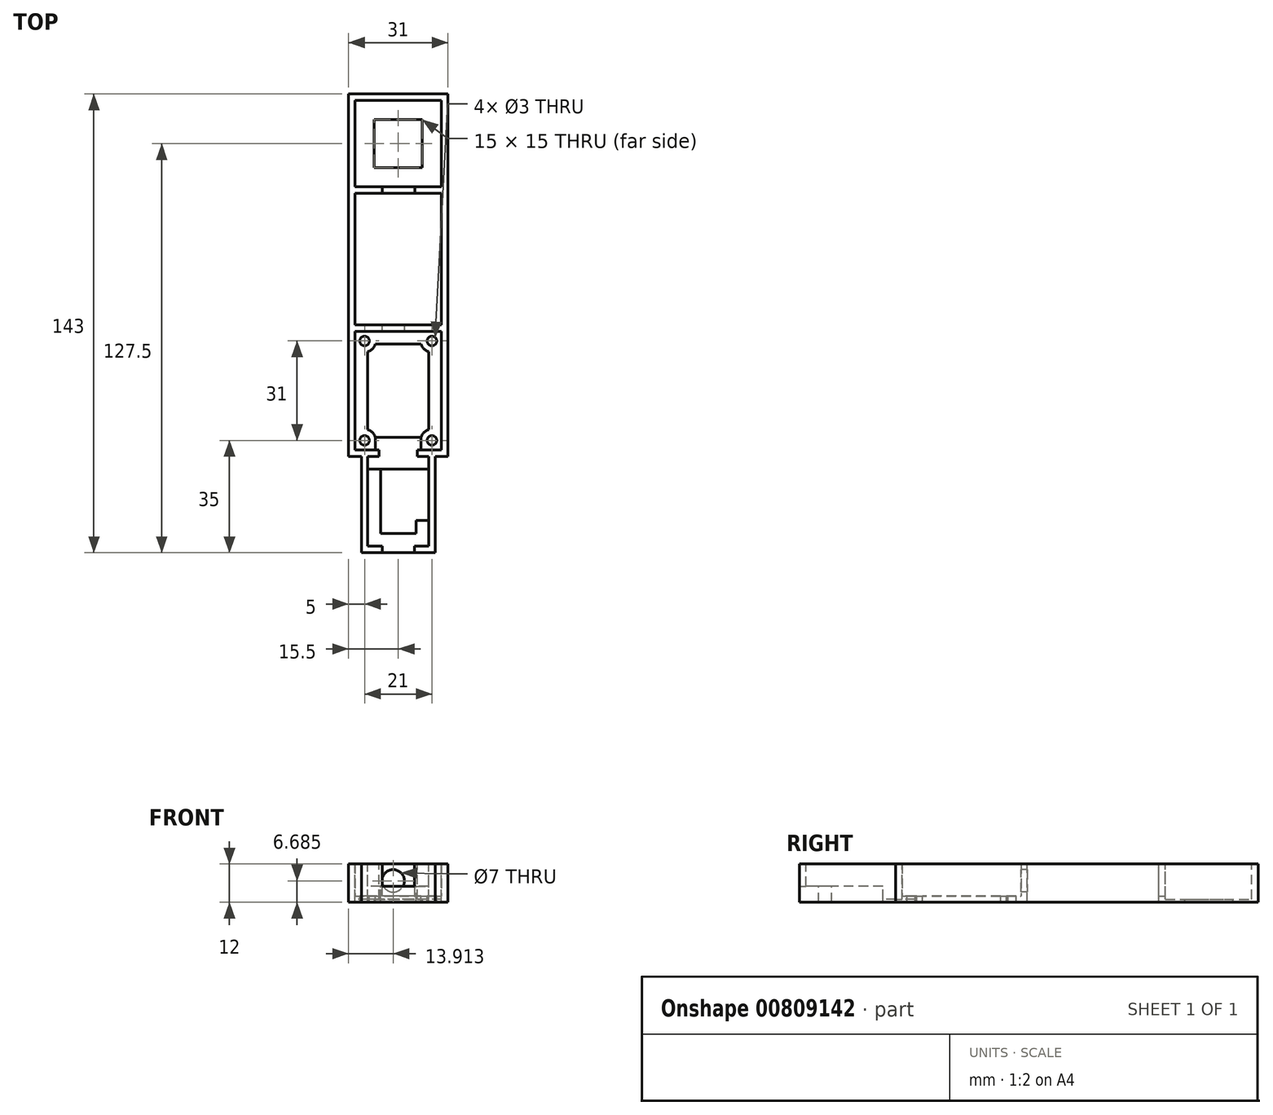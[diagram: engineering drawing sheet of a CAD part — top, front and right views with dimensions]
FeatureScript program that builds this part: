
annotation { "Feature Type Name" : "Feature", "Feature Type Description" : "" }
export const myFeature = defineFeature(function(context is Context, id is Id, definition is map)
    precondition{}
    {
        {
            var Q0;
            Q0=qCreatedBy(makeId("Top.planeOp"),FACE);
            var sketch = newSketch(context, id + "F0", { "sketchPlane" : qUnion([Q0])});
            skLineSegment(sketch, "E0.bottom", {"start": v(0, 0) * mm, "end": v(31, 0) * mm});
            skLineSegment(sketch, "E0.top", {"start": v(0, 41) * mm, "end": v(31, 41) * mm});
            skLineSegment(sketch, "E0.left", {"start": v(0, 0) * mm, "end": v(0, 41) * mm});
            skLineSegment(sketch, "E0.right", {"start": v(31, 0) * mm, "end": v(31, 41) * mm});
            skSolve(sketch);
        }
        {
            var Q0;
            Q0 = qSketchRegion(id + "F0", true);
            extrude(context, id + "F1", {"entities" : qUnion([Q0]), "depth" : 12 * mm, "offsetDistance" : 25 * mm});
        }
        {
            var Q0;
            Q0=makeQuery(id+"F1.opExtrude","CAP_FACE",FACE,{"disambiguationData":[OSD([sQuery(id+"F0.wireOp",EDGE,"E0.bottom"),sQuery(id+"F0.wireOp",EDGE,"E0.top"),sQuery(id+"F0.wireOp",EDGE,"E0.left"),sQuery(id+"F0.wireOp",EDGE,"E0.right")])],"isStart":false});
            shell(context, id + "F2", {"entities" : qUnion([Q0]), "thickness" : 2 * mm});
        }
        {
            var Q0;
            Q0=makeQuery(id+"F2.opShell","OFFSET_FACE",FACE,{"disambiguationData":[OSD([sQuery(id+"F0.wireOp",EDGE,"E0.bottom"),sQuery(id+"F0.wireOp",EDGE,"E0.top"),sQuery(id+"F0.wireOp",EDGE,"E0.left"),sQuery(id+"F0.wireOp",EDGE,"E0.right")])]});
            var sketch = newSketch(context, id + "F3", { "sketchPlane" : qUnion([Q0])});
            skLineSegment(sketch, "E1.bottom", {"start": v(26, 36) * mm, "end": v(5, 36) * mm, "construction": true});
            skLineSegment(sketch, "E1.top", {"start": v(26, 5) * mm, "end": v(5, 5) * mm, "construction": true});
            skLineSegment(sketch, "E1.left", {"start": v(26, 36) * mm, "end": v(26, 5) * mm, "construction": true});
            skLineSegment(sketch, "E1.right", {"start": v(5, 36) * mm, "end": v(5, 5) * mm, "construction": true});
            skCircle(sketch, "E2", {"center": v(5, 36) * mm, "radius": 1.5 * mm});
            skLineSegment(sketch, "E3", {"start": v(15.5, 39) * mm, "end": v(15.5, 2) * mm, "construction": true});
            skLineSegment(sketch, "E4", {"start": v(15.5, 2) * mm, "end": v(29, 20.5) * mm, "construction": true});
            skLineSegment(sketch, "E5", {"start": v(29, 20.5) * mm, "end": v(2, 20.5) * mm, "construction": true});
            skCircle(sketch, "E6", {"center": v(26, 36) * mm, "radius": 1.5 * mm});
            skCircle(sketch, "E7", {"center": v(26, 5) * mm, "radius": 1.5 * mm});
            skCircle(sketch, "E8", {"center": v(5, 5) * mm, "radius": 1.5 * mm});
            skSolve(sketch);
        }
        {
            var Q0;
            Q0 = qSketchRegion(id + "F3", true);
            extrude(context, id + "F4", {"entities" : qUnion([Q0]), "operationType" : NewBodyOperationType.REMOVE, "oppositeDirection" : true, "depth" : 25 * mm, "offsetDistance" : 25 * mm});
        }
        {
            var Q0;
            Q0=makeQuery(id+"F2.opShell","OFFSET_FACE",FACE,{"disambiguationData":[OSD([sQuery(id+"F0.wireOp",EDGE,"E0.bottom"),sQuery(id+"F0.wireOp",EDGE,"E0.top"),sQuery(id+"F0.wireOp",EDGE,"E0.left"),sQuery(id+"F0.wireOp",EDGE,"E0.right")])]});
            var sketch = newSketch(context, id + "F5", { "sketchPlane" : qUnion([Q0])});
            skLineSegment(sketch, "E9.0", {"start": v(22.65, 35) * mm, "end": v(8.35, 35) * mm});
            skLineSegment(sketch, "E9.1", {"start": v(25, 8.35) * mm, "end": v(25, 32.65) * mm});
            skLineSegment(sketch, "E9.2", {"start": v(8.35, 6) * mm, "end": v(22.65, 6) * mm});
            skLineSegment(sketch, "E9.3", {"start": v(6, 32.65) * mm, "end": v(6, 8.35) * mm});
            skArc(sketch, "E10", {"start": v(6, 32.65) * mm, "mid": v(7.47, 33.53) * mm, "end": v(8.35, 35) * mm});
            skArc(sketch, "E11", {"start": v(8.35, 6) * mm, "mid": v(7.47, 7.47) * mm, "end": v(6, 8.35) * mm});
            skArc(sketch, "E12", {"start": v(25, 8.35) * mm, "mid": v(23.53, 7.47) * mm, "end": v(22.65, 6) * mm});
            skArc(sketch, "E13", {"start": v(22.65, 35) * mm, "mid": v(23.53, 33.53) * mm, "end": v(25, 32.65) * mm});
            skSolve(sketch);
        }
        {
            var Q0;
            Q0 = qSketchRegion(id + "F5", true);
            extrude(context, id + "F6", {"entities" : qUnion([Q0]), "operationType" : NewBodyOperationType.REMOVE, "oppositeDirection" : true, "depth" : 25 * mm, "offsetDistance" : 25 * mm});
        }
        {
            var Q0;
            Q0=makeQuery(id+"F2.opShell","OFFSET_FACE",FACE,{"disambiguationData":[OSD([sQuery(id+"F0.wireOp",EDGE,"E0.bottom"),sQuery(id+"F0.wireOp",EDGE,"E0.top"),sQuery(id+"F0.wireOp",EDGE,"E0.left"),sQuery(id+"F0.wireOp",EDGE,"E0.right")])]});
            var sketch = newSketch(context, id + "F7", { "sketchPlane" : qUnion([Q0])});
            skLineSegment(sketch, "E14.bottom", {"start": v(8.35, 6) * mm, "end": v(22.65, 6) * mm});
            skLineSegment(sketch, "E14.top", {"start": v(8.35, 2) * mm, "end": v(22.65, 2) * mm});
            skLineSegment(sketch, "E14.left", {"start": v(8.35, 6) * mm, "end": v(8.35, 2) * mm});
            skLineSegment(sketch, "E14.right", {"start": v(22.65, 6) * mm, "end": v(22.65, 2) * mm});
            skSolve(sketch);
        }
        {
            var Q0;
            Q0 = qSketchRegion(id + "F7", true);
            extrude(context, id + "F8", {"entities" : qUnion([Q0]), "operationType" : NewBodyOperationType.REMOVE, "oppositeDirection" : true, "depth" : 1 * mm, "offsetDistance" : 25 * mm});
        }
        {
            var Q0;
            Q0=makeQuery(id+"F1.opExtrude","CAP_FACE",FACE,{"disambiguationData":[OSD([sQuery(id+"F0.wireOp",EDGE,"E0.bottom"),sQuery(id+"F0.wireOp",EDGE,"E0.top"),sQuery(id+"F0.wireOp",EDGE,"E0.left"),sQuery(id+"F0.wireOp",EDGE,"E0.right")])],"isStart":false});
            var sketch = newSketch(context, id + "F9", { "sketchPlane" : qUnion([Q0])});
            skLineSegment(sketch, "E15.bottom", {"start": v(9.5, 0) * mm, "end": v(21.5, 0) * mm});
            skLineSegment(sketch, "E15.top", {"start": v(9.5, 2) * mm, "end": v(21.5, 2) * mm});
            skLineSegment(sketch, "E15.left", {"start": v(9.5, 0) * mm, "end": v(9.5, 2) * mm});
            skLineSegment(sketch, "E15.right", {"start": v(21.5, 0) * mm, "end": v(21.5, 2) * mm});
            skSolve(sketch);
        }
        {
            var Q0;
            Q0 = qSketchRegion(id + "F9", true);
            extrude(context, id + "F10", {"entities" : qUnion([Q0]), "operationType" : NewBodyOperationType.REMOVE, "oppositeDirection" : true, "depth" : 11 * mm, "offsetDistance" : 25 * mm});
        }
        {
            var Q0;
            Q0=makeQuery(id+"F1.opExtrude","CAP_FACE",FACE,{"disambiguationData":[OSD([sQuery(id+"F0.wireOp",EDGE,"E0.bottom"),sQuery(id+"F0.wireOp",EDGE,"E0.top"),sQuery(id+"F0.wireOp",EDGE,"E0.left"),sQuery(id+"F0.wireOp",EDGE,"E0.right")])],"isStart":true});
            var sketch = newSketch(context, id + "F11", { "sketchPlane" : qUnion([Q0])});
            skLineSegment(sketch, "E16.bottom", {"start": v(27, 0) * mm, "end": v(4, 0) * mm});
            skLineSegment(sketch, "E16.top", {"start": v(27, 30) * mm, "end": v(4, 30) * mm});
            skLineSegment(sketch, "E16.left", {"start": v(27, 0) * mm, "end": v(27, 30) * mm});
            skLineSegment(sketch, "E16.right", {"start": v(4, 0) * mm, "end": v(4, 30) * mm});
            skSolve(sketch);
        }
        {
            var Q0;
            Q0 = qSketchRegion(id + "F11", true);
            extrude(context, id + "F12", {"entities" : qUnion([Q0]), "operationType" : NewBodyOperationType.ADD, "oppositeDirection" : true, "depth" : 12 * mm, "offsetDistance" : 25 * mm});
        }
        {
            var Q0;
            Q0=makeQuery(id+"F12.boolean.opBoolean","MERGE",FACE,{"derivedFrom":[makeQuery(id+"F1.opExtrude","CAP_FACE",FACE,{"disambiguationData":[OSD([sQuery(id+"F0.wireOp",EDGE,"E0.bottom"),sQuery(id+"F0.wireOp",EDGE,"E0.top"),sQuery(id+"F0.wireOp",EDGE,"E0.left"),sQuery(id+"F0.wireOp",EDGE,"E0.right")])],"isStart":false}),makeQuery(id+"F12.opExtrude","CAP_FACE",FACE,{"disambiguationData":[OSD([sQuery(id+"F11.wireOp",EDGE,"E16.bottom"),sQuery(id+"F11.wireOp",EDGE,"E16.top"),sQuery(id+"F11.wireOp",EDGE,"E16.left"),sQuery(id+"F11.wireOp",EDGE,"E16.right")])],"isStart":false})]});
            var sketch = newSketch(context, id + "F13", { "sketchPlane" : qUnion([Q0])});
            skLineSegment(sketch, "E17.bottom", {"start": v(25, 0) * mm, "end": v(6, 0) * mm});
            skLineSegment(sketch, "E17.top", {"start": v(25, -28) * mm, "end": v(6, -28) * mm});
            skLineSegment(sketch, "E17.left", {"start": v(25, 0) * mm, "end": v(25, -28) * mm});
            skLineSegment(sketch, "E17.right", {"start": v(6, 0) * mm, "end": v(6, -28) * mm});
            skSolve(sketch);
        }
        {
            var Q0;
            Q0 = qSketchRegion(id + "F13", true);
            extrude(context, id + "F14", {"entities" : qUnion([Q0]), "operationType" : NewBodyOperationType.REMOVE, "oppositeDirection" : true, "depth" : 7 * mm, "offsetDistance" : 25 * mm});
        }
        {
            var Q0;
            Q0=makeQuery(id+"F14.boolean.opBoolean","COPY",FACE,{"derivedFrom":makeQuery(id+"F14.opExtrude","CAP_FACE",FACE,{"disambiguationData":[OSD([sQuery(id+"F13.wireOp",EDGE,"E17.bottom"),sQuery(id+"F13.wireOp",EDGE,"E17.top"),sQuery(id+"F13.wireOp",EDGE,"E17.left"),sQuery(id+"F13.wireOp",EDGE,"E17.right")])],"isStart":false})});
            var sketch = newSketch(context, id + "F15", { "sketchPlane" : qUnion([Q0])});
            skLineSegment(sketch, "E18.bottom", {"start": v(25, 0) * mm, "end": v(6, 0) * mm});
            skLineSegment(sketch, "E18.top", {"start": v(25, -4) * mm, "end": v(6, -4) * mm});
            skLineSegment(sketch, "E18.left", {"start": v(25, 0) * mm, "end": v(25, -4) * mm});
            skLineSegment(sketch, "E18.right", {"start": v(6, 0) * mm, "end": v(6, -4) * mm});
            skSolve(sketch);
        }
        {
            var Q0;
            Q0 = qSketchRegion(id + "F15", true);
            extrude(context, id + "F16", {"entities" : qUnion([Q0]), "operationType" : NewBodyOperationType.REMOVE, "oppositeDirection" : true, "depth" : 4 * mm, "offsetDistance" : 25 * mm});
        }
        {
            var Q0;
            Q0=makeQuery(id+"F14.boolean.opBoolean","COPY",FACE,{"derivedFrom":makeQuery(id+"F14.opExtrude","CAP_FACE",FACE,{"disambiguationData":[OSD([sQuery(id+"F13.wireOp",EDGE,"E17.bottom"),sQuery(id+"F13.wireOp",EDGE,"E17.top"),sQuery(id+"F13.wireOp",EDGE,"E17.left"),sQuery(id+"F13.wireOp",EDGE,"E17.right")])],"isStart":false})});
            var sketch = newSketch(context, id + "F17", { "sketchPlane" : qUnion([Q0])});
            skLineSegment(sketch, "E19.bottom", {"start": v(21, -4) * mm, "end": v(10, -4) * mm});
            skLineSegment(sketch, "E19.top", {"start": v(21, -24) * mm, "end": v(10, -24) * mm});
            skLineSegment(sketch, "E19.left", {"start": v(21, -20) * mm, "end": v(21, -24) * mm});
            skLineSegment(sketch, "E19.right", {"start": v(10, -4) * mm, "end": v(10, -24) * mm});
            skLineSegment(sketch, "E20.bottom", {"start": v(21, -4) * mm, "end": v(25, -4) * mm});
            skLineSegment(sketch, "E20.top", {"start": v(21, -20) * mm, "end": v(25, -20) * mm});
            skLineSegment(sketch, "E20.right", {"start": v(25, -4) * mm, "end": v(25, -20) * mm});
            skSolve(sketch);
        }
        {
            var Q0;
            Q0 = qSketchRegion(id + "F17", true);
            extrude(context, id + "F18", {"entities" : qUnion([Q0]), "operationType" : NewBodyOperationType.REMOVE, "oppositeDirection" : true, "depth" : 25 * mm, "offsetDistance" : 25 * mm});
        }
        {
            var Q0;
            Q0=makeQuery(id+"F2.opShell","OFFSET_FACE",FACE,{"disambiguationData":[OSD([sQuery(id+"F0.wireOp",EDGE,"E0.top")])]});
            var sketch = newSketch(context, id + "F19", { "sketchPlane" : qUnion([Q0])});
            skCircle(sketch, "E21", {"center": v(13.91, 6.68) * mm, "radius": 3.5 * mm});
            skSolve(sketch);
        }
        {
            var Q0;
            Q0 = qSketchRegion(id + "F19", true);
            extrude(context, id + "F20", {"entities" : qUnion([Q0]), "operationType" : NewBodyOperationType.REMOVE, "oppositeDirection" : true, "depth" : 25 * mm, "offsetDistance" : 25 * mm});
        }
        {
            var Q0;
            Q0=makeQuery(id+"F12.boolean.opBoolean","MERGE",FACE,{"derivedFrom":[makeQuery(id+"F1.opExtrude","CAP_FACE",FACE,{"disambiguationData":[OSD([sQuery(id+"F0.wireOp",EDGE,"E0.bottom"),sQuery(id+"F0.wireOp",EDGE,"E0.top"),sQuery(id+"F0.wireOp",EDGE,"E0.left"),sQuery(id+"F0.wireOp",EDGE,"E0.right")])],"isStart":false}),makeQuery(id+"F12.opExtrude","CAP_FACE",FACE,{"disambiguationData":[OSD([sQuery(id+"F11.wireOp",EDGE,"E16.bottom"),sQuery(id+"F11.wireOp",EDGE,"E16.top"),sQuery(id+"F11.wireOp",EDGE,"E16.left"),sQuery(id+"F11.wireOp",EDGE,"E16.right")])],"isStart":false})]});
            var sketch = newSketch(context, id + "F21", { "sketchPlane" : qUnion([Q0])});
            skLineSegment(sketch, "E22", {"start": v(31, 41) * mm, "end": v(31, 113) * mm});
            skLineSegment(sketch, "E23", {"start": v(31, 113) * mm, "end": v(0, 113) * mm});
            skLineSegment(sketch, "E24", {"start": v(0, 113) * mm, "end": v(0, 41) * mm});
            skLineSegment(sketch, "E25", {"start": v(0, 41) * mm, "end": v(2, 41) * mm});
            skLineSegment(sketch, "E26", {"start": v(2, 41) * mm, "end": v(2, 82) * mm});
            skLineSegment(sketch, "E27", {"start": v(2, 111) * mm, "end": v(29, 111) * mm});
            skLineSegment(sketch, "E28", {"start": v(29, 111) * mm, "end": v(29, 84) * mm});
            skLineSegment(sketch, "E29", {"start": v(31, 41) * mm, "end": v(29, 41) * mm});
            skLineSegment(sketch, "E30.bottom", {"start": v(29, 82) * mm, "end": v(2, 82) * mm});
            skLineSegment(sketch, "E30.top", {"start": v(29, 84) * mm, "end": v(2, 84) * mm});
            skLineSegment(sketch, "E31.trimOffspring", {"start": v(29, 82) * mm, "end": v(29, 41) * mm});
            skLineSegment(sketch, "E32.trimOffspring", {"start": v(2, 84) * mm, "end": v(2, 111) * mm});
            skSolve(sketch);
        }
        {
            var Q0;
            Q0 = qSketchRegion(id + "F21", true);
            extrude(context, id + "F22", {"entities" : qUnion([Q0]), "operationType" : NewBodyOperationType.ADD, "oppositeDirection" : true, "depth" : 12 * mm, "offsetDistance" : 25 * mm});
        }
        {
            var Q0;
            Q0=makeQuery(id+"F22.boolean.opBoolean","MERGE",FACE,{"derivedFrom":[makeQuery(id+"F12.boolean.opBoolean","MERGE",FACE,{"derivedFrom":[makeQuery(id+"F1.opExtrude","CAP_FACE",FACE,{"disambiguationData":[OSD([sQuery(id+"F0.wireOp",EDGE,"E0.bottom"),sQuery(id+"F0.wireOp",EDGE,"E0.top"),sQuery(id+"F0.wireOp",EDGE,"E0.left"),sQuery(id+"F0.wireOp",EDGE,"E0.right")])],"isStart":true}),makeQuery(id+"F12.opExtrude","CAP_FACE",FACE,{"disambiguationData":[OSD([sQuery(id+"F11.wireOp",EDGE,"E16.bottom"),sQuery(id+"F11.wireOp",EDGE,"E16.top"),sQuery(id+"F11.wireOp",EDGE,"E16.left"),sQuery(id+"F11.wireOp",EDGE,"E16.right")])],"isStart":true})]}),makeQuery(id+"F22.opExtrude","CAP_FACE",FACE,{"disambiguationData":[OSD([sQuery(id+"F21.wireOp",EDGE,"E22"),sQuery(id+"F21.wireOp",EDGE,"E23"),sQuery(id+"F21.wireOp",EDGE,"E24"),sQuery(id+"F21.wireOp",EDGE,"E25"),sQuery(id+"F21.wireOp",EDGE,"E26"),sQuery(id+"F21.wireOp",EDGE,"E27"),sQuery(id+"F21.wireOp",EDGE,"E28"),sQuery(id+"F21.wireOp",EDGE,"E29"),sQuery(id+"F21.wireOp",EDGE,"E30.bottom"),sQuery(id+"F21.wireOp",EDGE,"E30.top"),sQuery(id+"F21.wireOp",EDGE,"E31.trimOffspring"),sQuery(id+"F21.wireOp",EDGE,"E32.trimOffspring")])],"isStart":false})]});
            var sketch = newSketch(context, id + "F23", { "sketchPlane" : qUnion([Q0])});
            skLineSegment(sketch, "E33.bottom", {"start": v(2, -84) * mm, "end": v(29, -84) * mm});
            skLineSegment(sketch, "E33.top", {"start": v(2, -111) * mm, "end": v(29, -111) * mm});
            skLineSegment(sketch, "E33.left", {"start": v(2, -84) * mm, "end": v(2, -111) * mm});
            skLineSegment(sketch, "E33.right", {"start": v(29, -84) * mm, "end": v(29, -111) * mm});
            skLineSegment(sketch, "E34.0", {"start": v(8, -90) * mm, "end": v(23, -90) * mm});
            skLineSegment(sketch, "E34.1", {"start": v(8, -90) * mm, "end": v(8, -105) * mm});
            skLineSegment(sketch, "E34.2", {"start": v(8, -105) * mm, "end": v(23, -105) * mm});
            skLineSegment(sketch, "E34.3", {"start": v(23, -90) * mm, "end": v(23, -105) * mm});
            skSolve(sketch);
        }
        {
            var Q0;
            Q0 = qSketchRegion(id + "F23", true);
            extrude(context, id + "F24", {"entities" : qUnion([Q0]), "operationType" : NewBodyOperationType.ADD, "oppositeDirection" : true, "depth" : 1 * mm, "offsetDistance" : 25 * mm});
        }
        {
            var Q0;
            Q0=makeQuery(id+"F22.boolean.opBoolean","MERGE",FACE,{"derivedFrom":[makeQuery(id+"F12.boolean.opBoolean","MERGE",FACE,{"derivedFrom":[makeQuery(id+"F1.opExtrude","CAP_FACE",FACE,{"disambiguationData":[OSD([sQuery(id+"F0.wireOp",EDGE,"E0.bottom"),sQuery(id+"F0.wireOp",EDGE,"E0.top"),sQuery(id+"F0.wireOp",EDGE,"E0.left"),sQuery(id+"F0.wireOp",EDGE,"E0.right")])],"isStart":false}),makeQuery(id+"F12.opExtrude","CAP_FACE",FACE,{"disambiguationData":[OSD([sQuery(id+"F11.wireOp",EDGE,"E16.bottom"),sQuery(id+"F11.wireOp",EDGE,"E16.top"),sQuery(id+"F11.wireOp",EDGE,"E16.left"),sQuery(id+"F11.wireOp",EDGE,"E16.right")])],"isStart":false})]}),makeQuery(id+"F22.opExtrude","CAP_FACE",FACE,{"disambiguationData":[OSD([sQuery(id+"F21.wireOp",EDGE,"E22"),sQuery(id+"F21.wireOp",EDGE,"E23"),sQuery(id+"F21.wireOp",EDGE,"E24"),sQuery(id+"F21.wireOp",EDGE,"E25"),sQuery(id+"F21.wireOp",EDGE,"E26"),sQuery(id+"F21.wireOp",EDGE,"E27"),sQuery(id+"F21.wireOp",EDGE,"E28"),sQuery(id+"F21.wireOp",EDGE,"E29"),sQuery(id+"F21.wireOp",EDGE,"E30.bottom"),sQuery(id+"F21.wireOp",EDGE,"E30.top"),sQuery(id+"F21.wireOp",EDGE,"E31.trimOffspring"),sQuery(id+"F21.wireOp",EDGE,"E32.trimOffspring")])],"isStart":true})]});
            var sketch = newSketch(context, id + "F25", { "sketchPlane" : qUnion([Q0])});
            skLineSegment(sketch, "E35.bottom", {"start": v(20.62, 82) * mm, "end": v(10.47, 82) * mm});
            skLineSegment(sketch, "E35.top", {"start": v(20.62, 84) * mm, "end": v(10.47, 84) * mm});
            skLineSegment(sketch, "E35.left", {"start": v(20.62, 82) * mm, "end": v(20.62, 84) * mm});
            skLineSegment(sketch, "E35.right", {"start": v(10.47, 82) * mm, "end": v(10.47, 84) * mm});
            skSolve(sketch);
        }
        {
            var Q0;
            Q0 = qSketchRegion(id + "F25", true);
            extrude(context, id + "F26", {"entities" : qUnion([Q0]), "operationType" : NewBodyOperationType.REMOVE, "oppositeDirection" : true, "depth" : 10 * mm, "offsetDistance" : 25 * mm});
        }
        {
            var Q0;
            Q0=makeQuery(id+"F22.boolean.opBoolean","MERGE",FACE,{"derivedFrom":[makeQuery(id+"F12.boolean.opBoolean","MERGE",FACE,{"derivedFrom":[makeQuery(id+"F1.opExtrude","CAP_FACE",FACE,{"disambiguationData":[OSD([sQuery(id+"F0.wireOp",EDGE,"E0.bottom"),sQuery(id+"F0.wireOp",EDGE,"E0.top"),sQuery(id+"F0.wireOp",EDGE,"E0.left"),sQuery(id+"F0.wireOp",EDGE,"E0.right")])],"isStart":false}),makeQuery(id+"F12.opExtrude","CAP_FACE",FACE,{"disambiguationData":[OSD([sQuery(id+"F11.wireOp",EDGE,"E16.bottom"),sQuery(id+"F11.wireOp",EDGE,"E16.top"),sQuery(id+"F11.wireOp",EDGE,"E16.left"),sQuery(id+"F11.wireOp",EDGE,"E16.right")])],"isStart":false})]}),makeQuery(id+"F22.opExtrude","CAP_FACE",FACE,{"disambiguationData":[OSD([sQuery(id+"F21.wireOp",EDGE,"E22"),sQuery(id+"F21.wireOp",EDGE,"E23"),sQuery(id+"F21.wireOp",EDGE,"E24"),sQuery(id+"F21.wireOp",EDGE,"E25"),sQuery(id+"F21.wireOp",EDGE,"E26"),sQuery(id+"F21.wireOp",EDGE,"E27"),sQuery(id+"F21.wireOp",EDGE,"E28"),sQuery(id+"F21.wireOp",EDGE,"E29"),sQuery(id+"F21.wireOp",EDGE,"E30.bottom"),sQuery(id+"F21.wireOp",EDGE,"E30.top"),sQuery(id+"F21.wireOp",EDGE,"E31.trimOffspring"),sQuery(id+"F21.wireOp",EDGE,"E32.trimOffspring")])],"isStart":true})]});
            var sketch = newSketch(context, id + "F27", { "sketchPlane" : qUnion([Q0])});
            skLineSegment(sketch, "E36.bottom", {"start": v(20.5, -30) * mm, "end": v(10.5, -30) * mm});
            skLineSegment(sketch, "E36.top", {"start": v(20.5, -28) * mm, "end": v(10.5, -28) * mm});
            skLineSegment(sketch, "E36.left", {"start": v(20.5, -30) * mm, "end": v(20.5, -28) * mm});
            skLineSegment(sketch, "E36.right", {"start": v(10.5, -30) * mm, "end": v(10.5, -28) * mm});
            skSolve(sketch);
        }
        {
            var Q0;
            Q0 = qSketchRegion(id + "F27", true);
            extrude(context, id + "F28", {"entities" : qUnion([Q0]), "operationType" : NewBodyOperationType.REMOVE, "oppositeDirection" : true, "depth" : 7 * mm, "offsetDistance" : 25 * mm});
        }
    });
